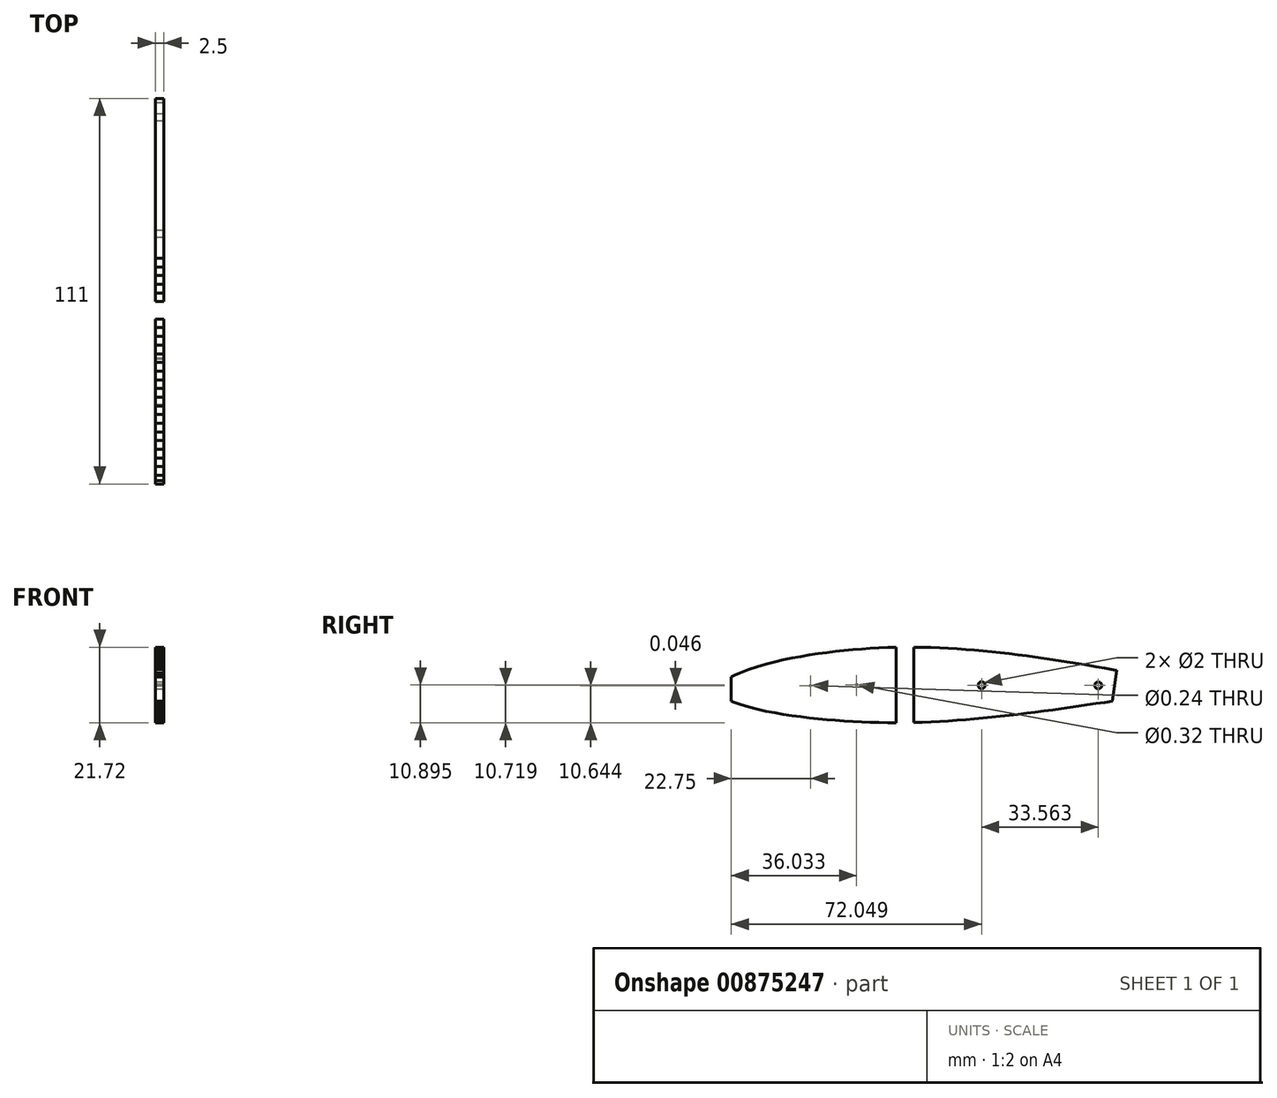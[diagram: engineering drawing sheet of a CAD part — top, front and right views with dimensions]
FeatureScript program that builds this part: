
annotation { "Feature Type Name" : "Feature", "Feature Type Description" : "" }
export const myFeature = defineFeature(function(context is Context, id is Id, definition is map)
    precondition{}
    {
        {
            var Q0;
            Q0=qCreatedBy(makeId("Right.planeOp"),FACE);
            var sketch = newSketch(context, id + "F0", { "sketchPlane" : qUnion([Q0])});
            skLineSegment(sketch, "E0", {"start": v(-55.5, 2.35) * mm, "end": v(-55.5, -4.7) * mm});
            skLineSegment(sketch, "E1", {"start": v(-8.02, -10.86) * mm, "end": v(-8.02, 10.82) * mm});
            skLineSegment(sketch, "E2", {"start": v(55.5, 4.18) * mm, "end": v(54.17, -4.68) * mm});
            skLineSegment(sketch, "E3", {"start": v(-3.02, -10.8) * mm, "end": v(-0.52, -10.73) * mm});
            skLineSegment(sketch, "E4", {"start": v(-0.52, -10.73) * mm, "end": v(1.98, -10.63) * mm});
            skLineSegment(sketch, "E5", {"start": v(19.48, -9.3) * mm, "end": v(21.98, -9.04) * mm});
            skLineSegment(sketch, "E6", {"start": v(29.48, -8.15) * mm, "end": v(31.98, -7.84) * mm});
            skLineSegment(sketch, "E7", {"start": v(46.99, -5.74) * mm, "end": v(49.49, -5.37) * mm});
            skLineSegment(sketch, "E8", {"start": v(26.98, -8.46) * mm, "end": v(29.48, -8.15) * mm});
            skLineSegment(sketch, "E9", {"start": v(21.98, -9.04) * mm, "end": v(24.48, -8.76) * mm});
            skLineSegment(sketch, "E10", {"start": v(49.49, -5.37) * mm, "end": v(51.99, -5) * mm});
            skLineSegment(sketch, "E11", {"start": v(9.48, -10.2) * mm, "end": v(11.98, -10) * mm});
            skLineSegment(sketch, "E12", {"start": v(6.98, -10.36) * mm, "end": v(9.48, -10.2) * mm});
            skLineSegment(sketch, "E13", {"start": v(31.98, -7.84) * mm, "end": v(34.48, -7.5) * mm});
            skLineSegment(sketch, "E14", {"start": v(14.48, -9.79) * mm, "end": v(16.98, -9.55) * mm});
            skLineSegment(sketch, "E15", {"start": v(41.98, -6.46) * mm, "end": v(44.49, -6.1) * mm});
            skLineSegment(sketch, "E16", {"start": v(16.98, -9.55) * mm, "end": v(19.48, -9.3) * mm});
            skLineSegment(sketch, "E17", {"start": v(36.98, -7.17) * mm, "end": v(39.48, -6.82) * mm});
            skLineSegment(sketch, "E18", {"start": v(1.98, -10.63) * mm, "end": v(4.48, -10.5) * mm});
            skLineSegment(sketch, "E19", {"start": v(39.48, -6.82) * mm, "end": v(41.98, -6.46) * mm});
            skLineSegment(sketch, "E20", {"start": v(11.98, -10) * mm, "end": v(14.48, -9.79) * mm});
            skLineSegment(sketch, "E21", {"start": v(44.49, -6.1) * mm, "end": v(46.99, -5.74) * mm});
            skLineSegment(sketch, "E22", {"start": v(51.99, -5) * mm, "end": v(54.17, -4.68) * mm});
            skLineSegment(sketch, "E23", {"start": v(4.48, -10.5) * mm, "end": v(6.98, -10.36) * mm});
            skLineSegment(sketch, "E24", {"start": v(24.48, -8.76) * mm, "end": v(26.98, -8.46) * mm});
            skLineSegment(sketch, "E25", {"start": v(34.48, -7.5) * mm, "end": v(36.98, -7.17) * mm});
            skLineSegment(sketch, "E26", {"start": v(21.98, 9.29) * mm, "end": v(24.48, 9) * mm});
            skLineSegment(sketch, "E27", {"start": v(9.48, 10.4) * mm, "end": v(11.98, 10.23) * mm});
            skLineSegment(sketch, "E28", {"start": v(26.98, 8.7) * mm, "end": v(29.48, 8.37) * mm});
            skLineSegment(sketch, "E29", {"start": v(24.48, 9) * mm, "end": v(26.98, 8.7) * mm});
            skLineSegment(sketch, "E30", {"start": v(19.48, 9.55) * mm, "end": v(21.98, 9.29) * mm});
            skLineSegment(sketch, "E31", {"start": v(16.98, 9.8) * mm, "end": v(19.48, 9.55) * mm});
            skLineSegment(sketch, "E32", {"start": v(1.98, 10.77) * mm, "end": v(4.48, 10.67) * mm});
            skLineSegment(sketch, "E33", {"start": v(11.98, 10.23) * mm, "end": v(14.48, 10.03) * mm});
            skLineSegment(sketch, "E34", {"start": v(6.98, 10.55) * mm, "end": v(9.48, 10.4) * mm});
            skLineSegment(sketch, "E35", {"start": v(-0.52, 10.83) * mm, "end": v(1.98, 10.77) * mm});
            skLineSegment(sketch, "E36", {"start": v(-3.02, 10.86) * mm, "end": v(-0.52, 10.83) * mm});
            skLineSegment(sketch, "E37", {"start": v(4.48, 10.67) * mm, "end": v(6.98, 10.55) * mm});
            skLineSegment(sketch, "E38", {"start": v(14.48, 10.03) * mm, "end": v(16.98, 9.8) * mm});
            skLineSegment(sketch, "E39", {"start": v(-35.53, -9.17) * mm, "end": v(-33.03, -9.48) * mm});
            skLineSegment(sketch, "E40", {"start": v(-33.03, -9.48) * mm, "end": v(-30.53, -9.75) * mm});
            skLineSegment(sketch, "E41", {"start": v(-48.03, -6.99) * mm, "end": v(-45.53, -7.54) * mm});
            skLineSegment(sketch, "E42", {"start": v(-54.53, -5.08) * mm, "end": v(-53.03, -5.6) * mm});
            skLineSegment(sketch, "E43", {"start": v(-25.53, -10.2) * mm, "end": v(-23.03, -10.37) * mm});
            skLineSegment(sketch, "E44", {"start": v(-53.03, -5.6) * mm, "end": v(-50.53, -6.35) * mm});
            skLineSegment(sketch, "E45", {"start": v(-15.53, -10.74) * mm, "end": v(-13.02, -10.8) * mm});
            skLineSegment(sketch, "E46", {"start": v(-10.52, -10.85) * mm, "end": v(-8.02, -10.86) * mm});
            skLineSegment(sketch, "E47", {"start": v(-38.03, -8.83) * mm, "end": v(-35.53, -9.17) * mm});
            skLineSegment(sketch, "E48", {"start": v(-18.03, -10.64) * mm, "end": v(-15.53, -10.74) * mm});
            skLineSegment(sketch, "E49", {"start": v(-45.53, -7.54) * mm, "end": v(-43.03, -8.03) * mm});
            skLineSegment(sketch, "E50", {"start": v(-55.5, -4.7) * mm, "end": v(-54.53, -5.08) * mm});
            skLineSegment(sketch, "E51", {"start": v(-43.03, -8.03) * mm, "end": v(-40.53, -8.45) * mm});
            skLineSegment(sketch, "E52", {"start": v(-20.53, -10.52) * mm, "end": v(-18.03, -10.64) * mm});
            skLineSegment(sketch, "E53", {"start": v(-40.53, -8.45) * mm, "end": v(-38.03, -8.83) * mm});
            skLineSegment(sketch, "E54", {"start": v(-28.03, -9.99) * mm, "end": v(-25.53, -10.2) * mm});
            skLineSegment(sketch, "E55", {"start": v(-23.03, -10.37) * mm, "end": v(-20.53, -10.52) * mm});
            skLineSegment(sketch, "E56", {"start": v(-50.53, -6.35) * mm, "end": v(-48.03, -6.99) * mm});
            skLineSegment(sketch, "E57", {"start": v(-13.02, -10.8) * mm, "end": v(-10.52, -10.85) * mm});
            skLineSegment(sketch, "E58", {"start": v(-30.53, -9.75) * mm, "end": v(-28.03, -9.99) * mm});
            skLineSegment(sketch, "E59", {"start": v(-50.53, 4.45) * mm, "end": v(-48.03, 5.27) * mm});
            skLineSegment(sketch, "E60", {"start": v(-55.5, 2.35) * mm, "end": v(-54.53, 2.83) * mm});
            skLineSegment(sketch, "E61", {"start": v(-18.03, 10.35) * mm, "end": v(-15.53, 10.52) * mm});
            skLineSegment(sketch, "E62", {"start": v(-43.03, 6.64) * mm, "end": v(-40.53, 7.22) * mm});
            skLineSegment(sketch, "E63", {"start": v(-38.03, 7.74) * mm, "end": v(-35.53, 8.2) * mm});
            skLineSegment(sketch, "E64", {"start": v(-30.53, 9) * mm, "end": v(-28.03, 9.35) * mm});
            skLineSegment(sketch, "E65", {"start": v(-53.03, 3.5) * mm, "end": v(-50.53, 4.45) * mm});
            skLineSegment(sketch, "E66", {"start": v(-13.02, 10.65) * mm, "end": v(-10.52, 10.76) * mm});
            skLineSegment(sketch, "E67", {"start": v(-35.53, 8.2) * mm, "end": v(-33.03, 8.63) * mm});
            skLineSegment(sketch, "E68", {"start": v(-54.53, 2.83) * mm, "end": v(-53.03, 3.5) * mm});
            skLineSegment(sketch, "E69", {"start": v(-33.03, 8.63) * mm, "end": v(-30.53, 9) * mm});
            skLineSegment(sketch, "E70", {"start": v(-28.03, 9.35) * mm, "end": v(-25.53, 9.65) * mm});
            skLineSegment(sketch, "E71", {"start": v(-10.52, 10.76) * mm, "end": v(-8.02, 10.82) * mm});
            skLineSegment(sketch, "E72", {"start": v(-23.03, 9.92) * mm, "end": v(-20.53, 10.16) * mm});
            skLineSegment(sketch, "E73", {"start": v(-45.53, 6) * mm, "end": v(-43.03, 6.64) * mm});
            skLineSegment(sketch, "E74", {"start": v(-25.53, 9.65) * mm, "end": v(-23.03, 9.92) * mm});
            skLineSegment(sketch, "E75", {"start": v(-40.53, 7.22) * mm, "end": v(-38.03, 7.74) * mm});
            skLineSegment(sketch, "E76", {"start": v(-48.03, 5.27) * mm, "end": v(-45.53, 6) * mm});
            skLineSegment(sketch, "E77", {"start": v(-15.53, 10.52) * mm, "end": v(-13.02, 10.65) * mm});
            skLineSegment(sketch, "E78", {"start": v(-20.53, 10.16) * mm, "end": v(-18.03, 10.35) * mm});
            skLineSegment(sketch, "E79", {"start": v(51.99, 4.8) * mm, "end": v(54.49, 4.36) * mm});
            skLineSegment(sketch, "E80", {"start": v(39.48, 6.9) * mm, "end": v(41.98, 6.5) * mm});
            skLineSegment(sketch, "E81", {"start": v(49.49, 5.25) * mm, "end": v(51.99, 4.8) * mm});
            skLineSegment(sketch, "E82", {"start": v(34.48, 7.67) * mm, "end": v(36.98, 7.3) * mm});
            skLineSegment(sketch, "E83", {"start": v(41.98, 6.5) * mm, "end": v(44.49, 6.1) * mm});
            skLineSegment(sketch, "E84", {"start": v(44.49, 6.1) * mm, "end": v(46.99, 5.68) * mm});
            skLineSegment(sketch, "E85", {"start": v(54.49, 4.36) * mm, "end": v(55.5, 4.18) * mm});
            skLineSegment(sketch, "E86", {"start": v(31.98, 8.02) * mm, "end": v(34.48, 7.67) * mm});
            skLineSegment(sketch, "E87", {"start": v(46.99, 5.68) * mm, "end": v(49.49, 5.25) * mm});
            skLineSegment(sketch, "E88", {"start": v(29.48, 8.37) * mm, "end": v(31.98, 8.02) * mm});
            skLineSegment(sketch, "E89", {"start": v(36.98, 7.3) * mm, "end": v(39.48, 6.9) * mm});
            skLineSegment(sketch, "E90", {"start": v(-3.02, 10.86) * mm, "end": v(-3.02, -10.8) * mm});
            skCircle(sketch, "E91", {"center": v(-32.75, -0.22) * mm, "radius": 0.12 * mm});
            skCircle(sketch, "E92", {"center": v(50.11, -0.14) * mm, "radius": 0.06 * mm});
            skCircle(sketch, "E93", {"center": v(-19.47, 0.04) * mm, "radius": 0.16 * mm});
            skCircle(sketch, "E94", {"center": v(16.55, -0.1) * mm, "radius": 0.06 * mm});
            skSolve(sketch);
        }
        {
            var Q0;
            Q0 = qSketchRegion(id + "F0", true);
            extrude(context, id + "F1", {"entities" : qUnion([Q0]), "depth" : 2.5 * mm, "offsetDistance" : 25 * mm});
        }
        {
            var Q0;
            Q0=makeQuery(id+"F1.opExtrude","CAP_FACE",FACE,{"disambiguationData":[OSD([sQuery(id+"F0.wireOp",EDGE,"E2"),sQuery(id+"F0.wireOp",EDGE,"E3"),sQuery(id+"F0.wireOp",EDGE,"E4"),sQuery(id+"F0.wireOp",EDGE,"E5"),sQuery(id+"F0.wireOp",EDGE,"E6"),sQuery(id+"F0.wireOp",EDGE,"E7"),sQuery(id+"F0.wireOp",EDGE,"E8"),sQuery(id+"F0.wireOp",EDGE,"E9"),sQuery(id+"F0.wireOp",EDGE,"E10"),sQuery(id+"F0.wireOp",EDGE,"E11"),sQuery(id+"F0.wireOp",EDGE,"E12"),sQuery(id+"F0.wireOp",EDGE,"E13"),sQuery(id+"F0.wireOp",EDGE,"E14"),sQuery(id+"F0.wireOp",EDGE,"E15"),sQuery(id+"F0.wireOp",EDGE,"E16"),sQuery(id+"F0.wireOp",EDGE,"E17"),sQuery(id+"F0.wireOp",EDGE,"E18"),sQuery(id+"F0.wireOp",EDGE,"E19"),sQuery(id+"F0.wireOp",EDGE,"E20"),sQuery(id+"F0.wireOp",EDGE,"E21"),sQuery(id+"F0.wireOp",EDGE,"E22"),sQuery(id+"F0.wireOp",EDGE,"E23"),sQuery(id+"F0.wireOp",EDGE,"E24"),sQuery(id+"F0.wireOp",EDGE,"E25"),sQuery(id+"F0.wireOp",EDGE,"E26"),sQuery(id+"F0.wireOp",EDGE,"E27"),sQuery(id+"F0.wireOp",EDGE,"E28"),sQuery(id+"F0.wireOp",EDGE,"E29"),sQuery(id+"F0.wireOp",EDGE,"E30"),sQuery(id+"F0.wireOp",EDGE,"E31"),sQuery(id+"F0.wireOp",EDGE,"E32"),sQuery(id+"F0.wireOp",EDGE,"E33"),sQuery(id+"F0.wireOp",EDGE,"E34"),sQuery(id+"F0.wireOp",EDGE,"E35"),sQuery(id+"F0.wireOp",EDGE,"E36"),sQuery(id+"F0.wireOp",EDGE,"E37"),sQuery(id+"F0.wireOp",EDGE,"E38"),sQuery(id+"F0.wireOp",EDGE,"E79"),sQuery(id+"F0.wireOp",EDGE,"E80"),sQuery(id+"F0.wireOp",EDGE,"E81"),sQuery(id+"F0.wireOp",EDGE,"E82"),sQuery(id+"F0.wireOp",EDGE,"E83"),sQuery(id+"F0.wireOp",EDGE,"E84"),sQuery(id+"F0.wireOp",EDGE,"E85"),sQuery(id+"F0.wireOp",EDGE,"E86"),sQuery(id+"F0.wireOp",EDGE,"E87"),sQuery(id+"F0.wireOp",EDGE,"E88"),sQuery(id+"F0.wireOp",EDGE,"E89"),sQuery(id+"F0.wireOp",EDGE,"E90"),sQuery(id+"F0.wireOp",EDGE,"E92"),sQuery(id+"F0.wireOp",EDGE,"E94")])],"isStart":false});
            var sketch = newSketch(context, id + "F2", { "sketchPlane" : qUnion([Q0])});
            skCircle(sketch, "E95", {"center": v(16.55, -0.1) * mm, "radius": 1 * mm});
            skCircle(sketch, "E96", {"center": v(50.11, -0.14) * mm, "radius": 1 * mm});
            skSolve(sketch);
        }
        {
            var Q0;
            Q0 = qSketchRegion(id + "F2", true);
            extrude(context, id + "F3", {"entities" : qUnion([Q0]), "operationType" : NewBodyOperationType.REMOVE, "endBound" : BoundingType.THROUGH_ALL, "oppositeDirection" : true, "depth" : 25 * mm, "offsetDistance" : 25 * mm});
        }
    });
